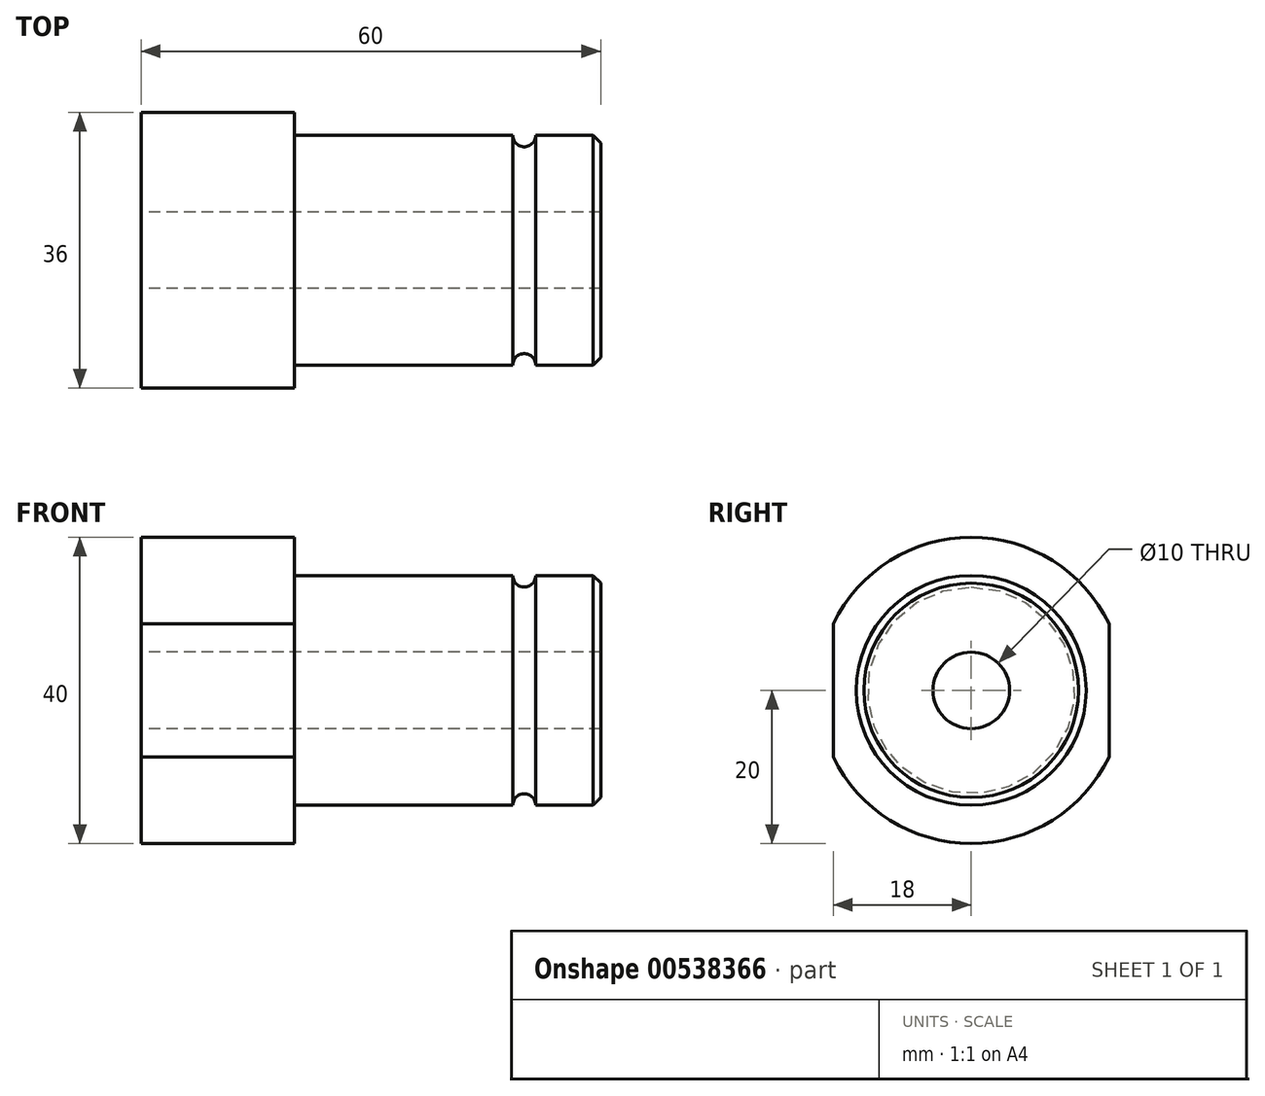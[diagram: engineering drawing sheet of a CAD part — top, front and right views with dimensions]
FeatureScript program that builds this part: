
annotation { "Feature Type Name" : "Feature", "Feature Type Description" : "" }
export const myFeature = defineFeature(function(context is Context, id is Id, definition is map)
    precondition{}
    {
        {
            var Q0;
            Q0=qCreatedBy(makeId("Front.planeOp"),FACE);
            var sketch = newSketch(context, id + "F0", { "sketchPlane" : qUnion([Q0])});
            skLineSegment(sketch, "E0", {"start": v(0, 0) * mm, "end": v(0, 20) * mm});
            skLineSegment(sketch, "E1", {"start": v(0, 20) * mm, "end": v(20, 20) * mm});
            skLineSegment(sketch, "E2", {"start": v(20, 20) * mm, "end": v(20, 15) * mm});
            skLineSegment(sketch, "E3", {"start": v(20, 15) * mm, "end": v(60, 15) * mm});
            skLineSegment(sketch, "E4", {"start": v(60, 15) * mm, "end": v(60, 0) * mm});
            skLineSegment(sketch, "E5", {"start": v(60, 0) * mm, "end": v(0, 0) * mm});
            skLineSegment(sketch, "E6", {"start": v(-3.57, 0) * mm, "end": v(30.31, 0) * mm, "construction": true});
            skPoint(sketch, "E6.endSnap0", {"position": v(30, 0) * mm});
            skSolve(sketch);
        }
        {
            var Q0;
            Q0=makeQuery(id+"F0.imprint","IMPRINT",FACE,{"disambiguationData":[TD([[makeQuery(id+"F0.imprint","IMPRINT",EDGE,{"derivedFrom":sQuery(id+"F0.wireOp",EDGE,"E0")}),-1.0]])]});
            var Q1;
            Q1=sQuery(id+"F0.wireOp",EDGE,"E6");
            revolve(context, id + "F1", {"entities" : qUnion([Q0]), "axis" : qUnion([Q1]), "revolveType" : RevolveType.FULL});
        }
        {
            var Q0;
            Q0=makeQuery(id+"F1.opRevolve","SWEPT_FACE",FACE,{"disambiguationData":[OSD([sQuery(id+"F0.wireOp",EDGE,"E0")])]});
            var sketch = newSketch(context, id + "F2", { "sketchPlane" : qUnion([Q0])});
            skCircle(sketch, "E7", {"center": v(0, 0) * mm, "radius": 5 * mm});
            skSolve(sketch);
        }
        {
            var Q0;
            Q0=makeQuery(id+"F2.imprint","IMPRINT",FACE,{"disambiguationData":[TD([[makeQuery(id+"F2.imprint","IMPRINT",EDGE,{"derivedFrom":sQuery(id+"F2.wireOp",EDGE,"E7")}),1.0]])]});
            extrude(context, id + "F3", {"entities" : qUnion([Q0]), "operationType" : NewBodyOperationType.REMOVE, "endBound" : BoundingType.THROUGH_ALL, "oppositeDirection" : true, "depth" : 25 * mm, "offsetDistance" : 25 * mm});
        }
        {
            var Q0;
            Q0=makeQuery(id+"F1.opRevolve","SWEPT_EDGE",EDGE,{"disambiguationData":[OSD([sQuery(id+"F0.wireOp",EDGE,"E3"),sQuery(id+"F0.wireOp",EDGE,"E4")])]});
            chamfer(context, id + "F4", {"entities" : qUnion([Q0]), "width" : 1 * mm, "tangentPropagation" : true});
        }
        {
            var Q0;
            Q0=makeQuery(id+"F1.opRevolve","SWEPT_FACE",FACE,{"disambiguationData":[OSD([sQuery(id+"F0.wireOp",EDGE,"E4")])]});
            cPlane(context, id + "F5", {"entities" : qUnion([Q0]), "cplaneType" : CPlaneType.OFFSET, "offset" : 10 * mm, "oppositeDirection" : true, "width" : 150 * mm, "height" : 150 * mm});
        }
        {
            var Q0;
            Q0=qCreatedBy(id+"F5.planeOp",FACE);
            var sketch = newSketch(context, id + "F6", { "sketchPlane" : qUnion([Q0])});
            skCircle(sketch, "E8", {"center": v(0, 0) * mm, "radius": 15 * mm});
            skSolve(sketch);
        }
        {
            var Q0;
            Q0=qCreatedBy(makeId("Front.planeOp"),FACE);
            var sketch = newSketch(context, id + "F7", { "sketchPlane" : qUnion([Q0])});
            skCircle(sketch, "E9", {"center": v(50, 15) * mm, "radius": 1.5 * mm});
            skSolve(sketch);
        }
        {
            var Q0;
            Q0=makeQuery(id+"F7.imprint","IMPRINT",FACE,{"disambiguationData":[TD([[makeQuery(id+"F7.imprint","IMPRINT",EDGE,{"derivedFrom":sQuery(id+"F7.wireOp",EDGE,"E9")}),1.0]])]});
            var Q1;
            Q1=sQuery(id+"F6.wireOp",EDGE,"E8");
            sweep(context, id + "F8", {"operationType" : NewBodyOperationType.REMOVE, "profiles" : qUnion([Q0]), "path" : qUnion([Q1])});
        }
        {
            var Q0;
            Q0=makeQuery(id+"F1.opRevolve","SWEPT_FACE",FACE,{"disambiguationData":[OSD([sQuery(id+"F0.wireOp",EDGE,"E0")])]});
            var sketch = newSketch(context, id + "F9", { "sketchPlane" : qUnion([Q0])});
            skLineSegment(sketch, "E10", {"start": v(18, 8.72) * mm, "end": v(18, -8.72) * mm});
            skLineSegment(sketch, "E11", {"start": v(-18, 8.72) * mm, "end": v(-18, -8.72) * mm});
            skSolve(sketch);
        }
        {
            var Q0;
            {var subQ0=sQuery(id+"F9.wireOp",EDGE,"E11");Q0=makeQuery(id+"F9.imprint","IMPRINT",FACE,{"disambiguationData":[TD([[makeQuery(id+"F9.imprint","IMPRINT",EDGE,{"derivedFrom":subQ0}),-1.0]])]});}
            var Q1;
            {var subQ0=sQuery(id+"F9.wireOp",EDGE,"E10");Q1=makeQuery(id+"F9.imprint","IMPRINT",FACE,{"disambiguationData":[TD([[makeQuery(id+"F9.imprint","IMPRINT",EDGE,{"derivedFrom":subQ0}),1.0]])]});}
            extrude(context, id + "F10", {"entities" : qUnion([Q0, Q1]), "operationType" : NewBodyOperationType.REMOVE, "endBound" : BoundingType.THROUGH_ALL, "oppositeDirection" : true, "depth" : 25 * mm, "offsetDistance" : 25 * mm});
        }
    });
